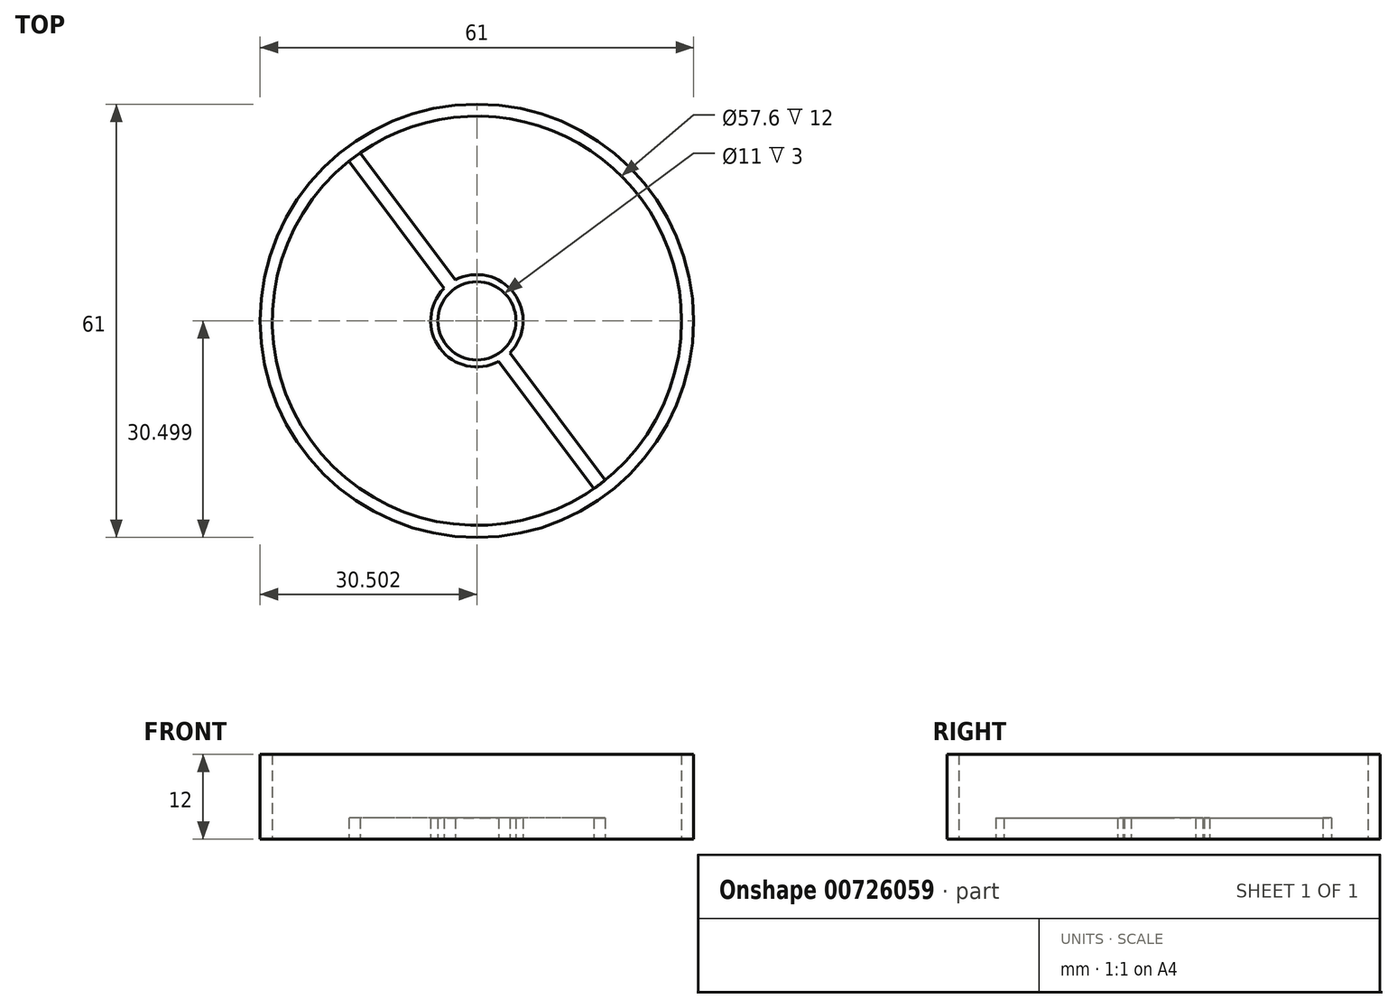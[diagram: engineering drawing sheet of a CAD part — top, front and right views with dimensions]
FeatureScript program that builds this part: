
annotation { "Feature Type Name" : "Feature", "Feature Type Description" : "" }
export const myFeature = defineFeature(function(context is Context, id is Id, definition is map)
    precondition{}
    {
        {
            var Q0;
            Q0=qCreatedBy(makeId("Top.planeOp"),FACE);
            var sketch = newSketch(context, id + "F0", { "sketchPlane" : qUnion([Q0])});
            skArc(sketch, "E0", {"start": v(-16.56, 23.8) * mm, "mid": v(-23.76, -16.3) * mm, "end": v(16.33, -23.5) * mm});
            skCircle(sketch, "E1", {"center": v(-0.12, 0.15) * mm, "radius": 30.5 * mm});
            skLineSegment(sketch, "E2", {"start": v(17.14, -22.9) * mm, "end": v(3.78, -5.05) * mm, "construction": true});
            skLineSegment(sketch, "E3.0", {"start": v(17.93, -22.3) * mm, "end": v(4.53, -4.4) * mm});
            skLineSegment(sketch, "E4.0", {"start": v(16.33, -23.5) * mm, "end": v(2.93, -5.6) * mm});
            skCircle(sketch, "E5", {"center": v(-0.12, 0.15) * mm, "radius": 5.5 * mm});
            skArc(sketch, "E6", {"start": v(-4.77, 4.7) * mm, "mid": v(-5.32, -3.75) * mm, "end": v(2.93, -5.6) * mm});
            skLineSegment(sketch, "E7.trimOffspring", {"start": v(-4.01, 5.35) * mm, "end": v(-17.38, 23.2) * mm, "construction": true});
            skLineSegment(sketch, "E8.trimOffspring", {"start": v(-3.17, 5.9) * mm, "end": v(-16.56, 23.8) * mm});
            skLineSegment(sketch, "E9.trimOffspring", {"start": v(-4.77, 4.7) * mm, "end": v(-18.17, 22.6) * mm});
            skArc(sketch, "E10.trimOffspring", {"start": v(16.33, -23.5) * mm, "mid": v(23.52, 16.6) * mm, "end": v(-16.56, 23.8) * mm});
            skArc(sketch, "E11.trimOffspring", {"start": v(4.53, -4.4) * mm, "mid": v(5.09, 4.04) * mm, "end": v(-3.17, 5.9) * mm});
            skSolve(sketch);
        }
        {
            var Q0;
            Q0 = qSketchRegion(id + "F0", true);
            extrude(context, id + "F1", {"entities" : qUnion([Q0]), "depth" : 12 * mm, "offsetDistance" : 25 * mm});
        }
        {
            var Q0;
            {var subQ1=sQuery(id+"F0.wireOp",EDGE,"E3.0");Q0=makeQuery(id+"F0.imprint","IMPRINT",FACE,{"disambiguationData":[TD([[makeQuery(id+"F0.imprint","IMPRINT",EDGE,{"derivedFrom":subQ1}),1.0]])]});}
            extrude(context, id + "F2", {"entities" : qUnion([Q0]), "operationType" : NewBodyOperationType.ADD, "depth" : 3 * mm, "offsetDistance" : 25 * mm});
        }
    });
